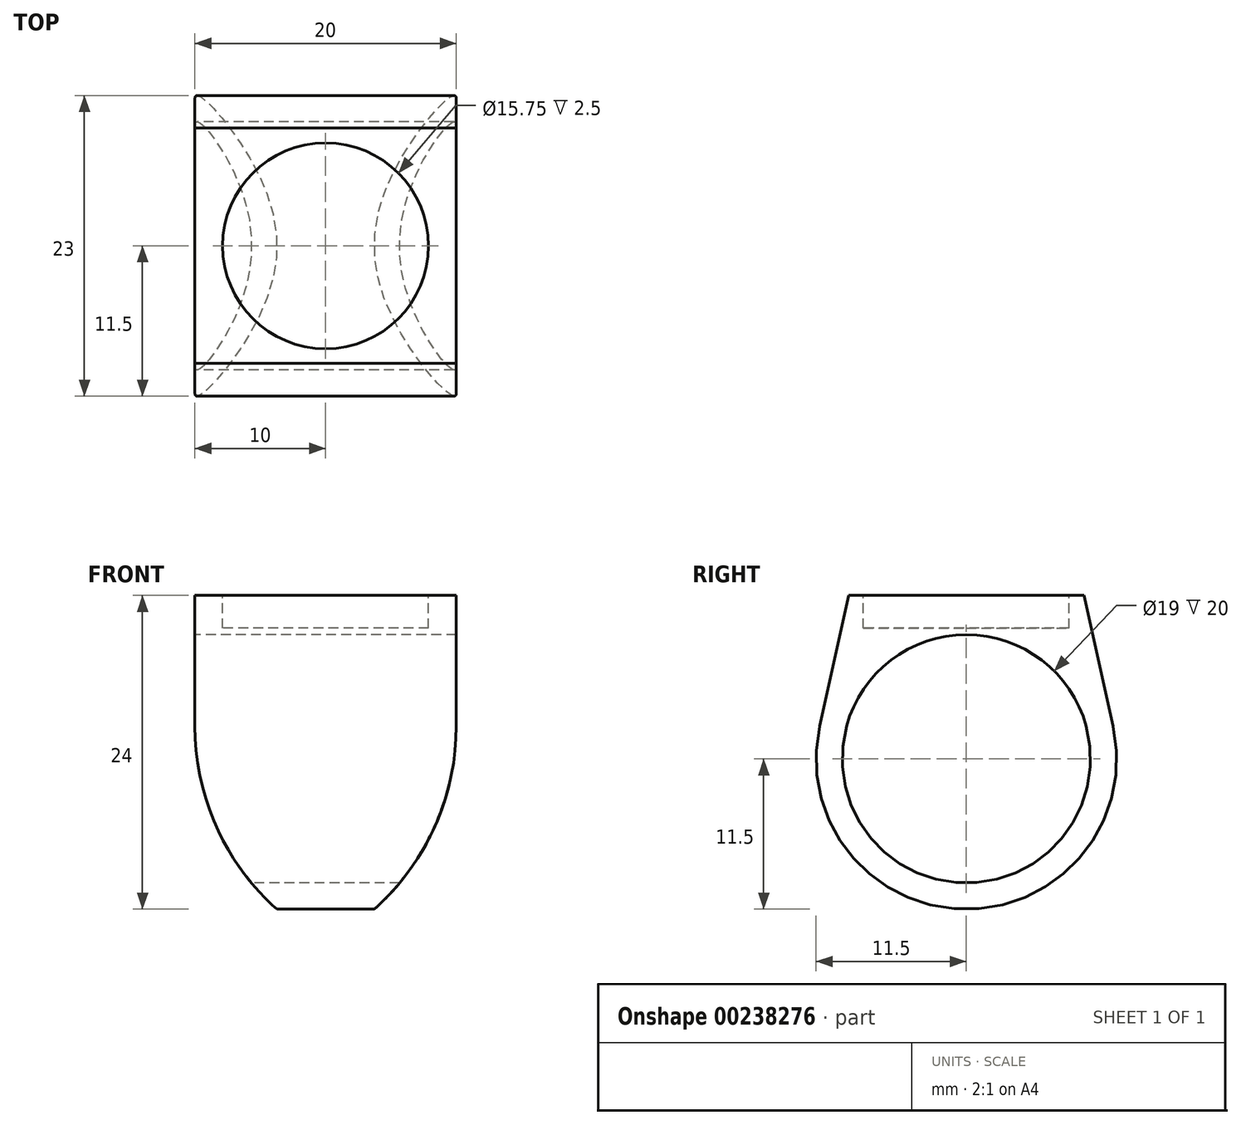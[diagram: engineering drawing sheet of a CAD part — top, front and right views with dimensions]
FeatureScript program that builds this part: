
annotation { "Feature Type Name" : "Feature", "Feature Type Description" : "" }
export const myFeature = defineFeature(function(context is Context, id is Id, definition is map)
    precondition{}
    {
        {
            var Q0;
            Q0=qCreatedBy(makeId("Right.planeOp"),FACE);
            var sketch = newSketch(context, id + "F0", { "sketchPlane" : qUnion([Q0])});
            skCircle(sketch, "E0", {"center": v(0, 0) * mm, "radius": 9.5 * mm});
            skCircle(sketch, "E1", {"center": v(0, 0) * mm, "radius": 11.5 * mm});
            skLineSegment(sketch, "E2", {"start": v(9, 12.5) * mm, "end": v(-9, 12.5) * mm});
            skLineSegment(sketch, "E3", {"start": v(-9, 12.5) * mm, "end": v(-11.23, 2.5) * mm});
            skLineSegment(sketch, "E4", {"start": v(9, 12.5) * mm, "end": v(11.23, 2.5) * mm});
            skPoint(sketch, "E5", {"position": v(0, 12.5) * mm});
            skSolve(sketch);
        }
        {
            var Q0;
            Q0=qSketchRegion(id+"F0",true);
            extrude(context, id + "F1", {"entities" : qUnion([Q0]), "endBound" : BoundingType.SYMMETRIC, "depth" : 20 * mm});
        }
        {
            var Q0;
            Q0=qCreatedBy(makeId("Front.planeOp"),FACE);
            var sketch = newSketch(context, id + "F2", { "sketchPlane" : qUnion([Q0])});
            skLineSegment(sketch, "E6", {"start": v(10, 2.5) * mm, "end": v(10, 12.5) * mm});
            skLineSegment(sketch, "E7", {"start": v(10, 12.5) * mm, "end": v(15, 12.5) * mm});
            skLineSegment(sketch, "E8", {"start": v(15, 12.5) * mm, "end": v(15, -17.5) * mm});
            skLineSegment(sketch, "E9", {"start": v(15, -17.5) * mm, "end": v(-15, -17.5) * mm});
            skLineSegment(sketch, "E10", {"start": v(-15, -17.5) * mm, "end": v(-15, 12.5) * mm});
            skLineSegment(sketch, "E11", {"start": v(-15, 12.5) * mm, "end": v(-10, 12.5) * mm});
            skLineSegment(sketch, "E12", {"start": v(-10, 12.5) * mm, "end": v(-10, 2.5) * mm});
            skArc(sketch, "E13", {"start": v(2.5, -12.5) * mm, "mid": v(8.02, -5.89) * mm, "end": v(10, 2.5) * mm});
            skArc(sketch, "E14", {"start": v(-10, 2.5) * mm, "mid": v(-8.02, -5.89) * mm, "end": v(-2.5, -12.5) * mm});
            skLineSegment(sketch, "E15", {"start": v(2.5, -12.5) * mm, "end": v(-2.5, -12.5) * mm});
            skPoint(sketch, "E16", {"position": v(0, -12.5) * mm});
            skSolve(sketch);
        }
        {
            var Q0;
            Q0=qSketchRegion(id+"F2",true);
            extrude(context, id + "F3", {"entities" : qUnion([Q0]), "operationType" : NewBodyOperationType.REMOVE, "endBound" : BoundingType.SYMMETRIC, "oppositeDirection" : true, "depth" : 30 * mm});
        }
        {
            var Q0;
            Q0=makeQuery(id+"F1.opExtrude","SWEPT_FACE",FACE,{"disambiguationData":[OSD([sQuery(id+"F0.wireOp",EDGE,"E2")])]});
            var sketch = newSketch(context, id + "F4", { "sketchPlane" : qUnion([Q0])});
            skCircle(sketch, "E17", {"center": v(0, 0) * mm, "radius": 7.88 * mm});
            skSolve(sketch);
        }
        {
            var Q0;
            Q0=qSketchRegion(id+"F4",true);
            extrude(context, id + "F5", {"entities" : qUnion([Q0]), "operationType" : NewBodyOperationType.REMOVE, "oppositeDirection" : true, "depth" : 2.5 * mm});
        }
    });
